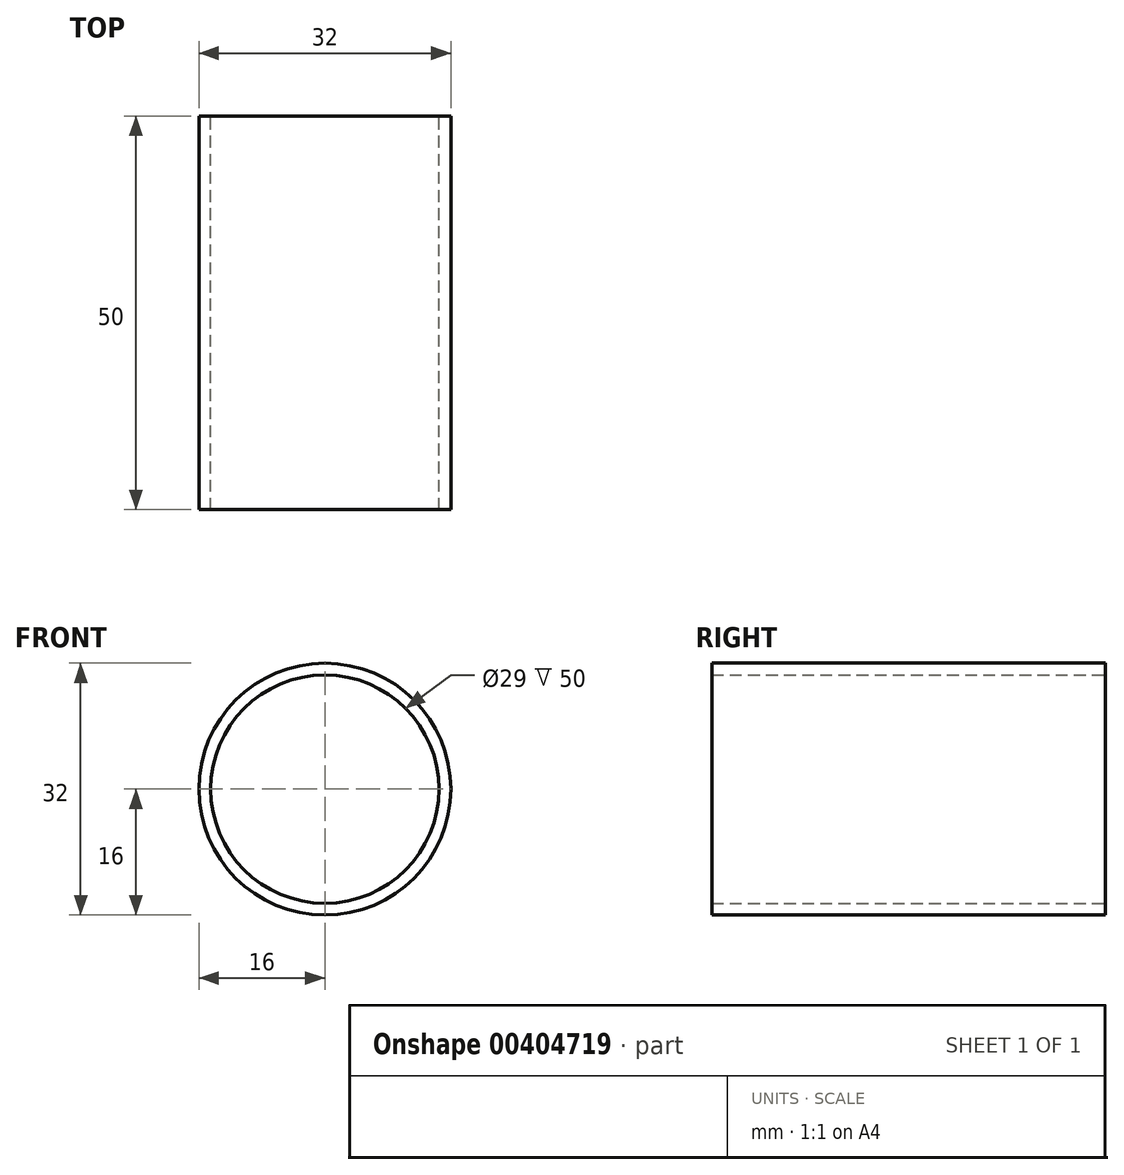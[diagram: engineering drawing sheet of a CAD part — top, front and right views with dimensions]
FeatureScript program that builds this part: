
annotation { "Feature Type Name" : "Feature", "Feature Type Description" : "" }
export const myFeature = defineFeature(function(context is Context, id is Id, definition is map)
    precondition{}
    {
        {
            var Q0;
            Q0=qCreatedBy(makeId("Front.planeOp"),FACE);
            var sketch = newSketch(context, id + "F0", { "sketchPlane" : qUnion([Q0])});
            skCircle(sketch, "E0", {"center": v(0, 0) * mm, "radius": 16 * mm});
            skCircle(sketch, "E1", {"center": v(0, 0) * mm, "radius": 14.5 * mm});
            skSolve(sketch);
        }
        {
            var Q0;
            Q0=makeQuery(id+"F0.imprint","IMPRINT",FACE,{"disambiguationData":[TD([[makeQuery(id+"F0.imprint","IMPRINT",EDGE,{"derivedFrom":sQuery(id+"F0.wireOp",EDGE,"E0")}),1.0]])]});
            extrude(context, id + "F1", {"entities" : qUnion([Q0]), "flatOperationType" : FlatOperationType.REMOVE, "offsetDistance" : 25 * mm, "depth" : 50 * mm, "domain" : OperationDomain.MODEL, "symmetric" : true});
        }
    });
